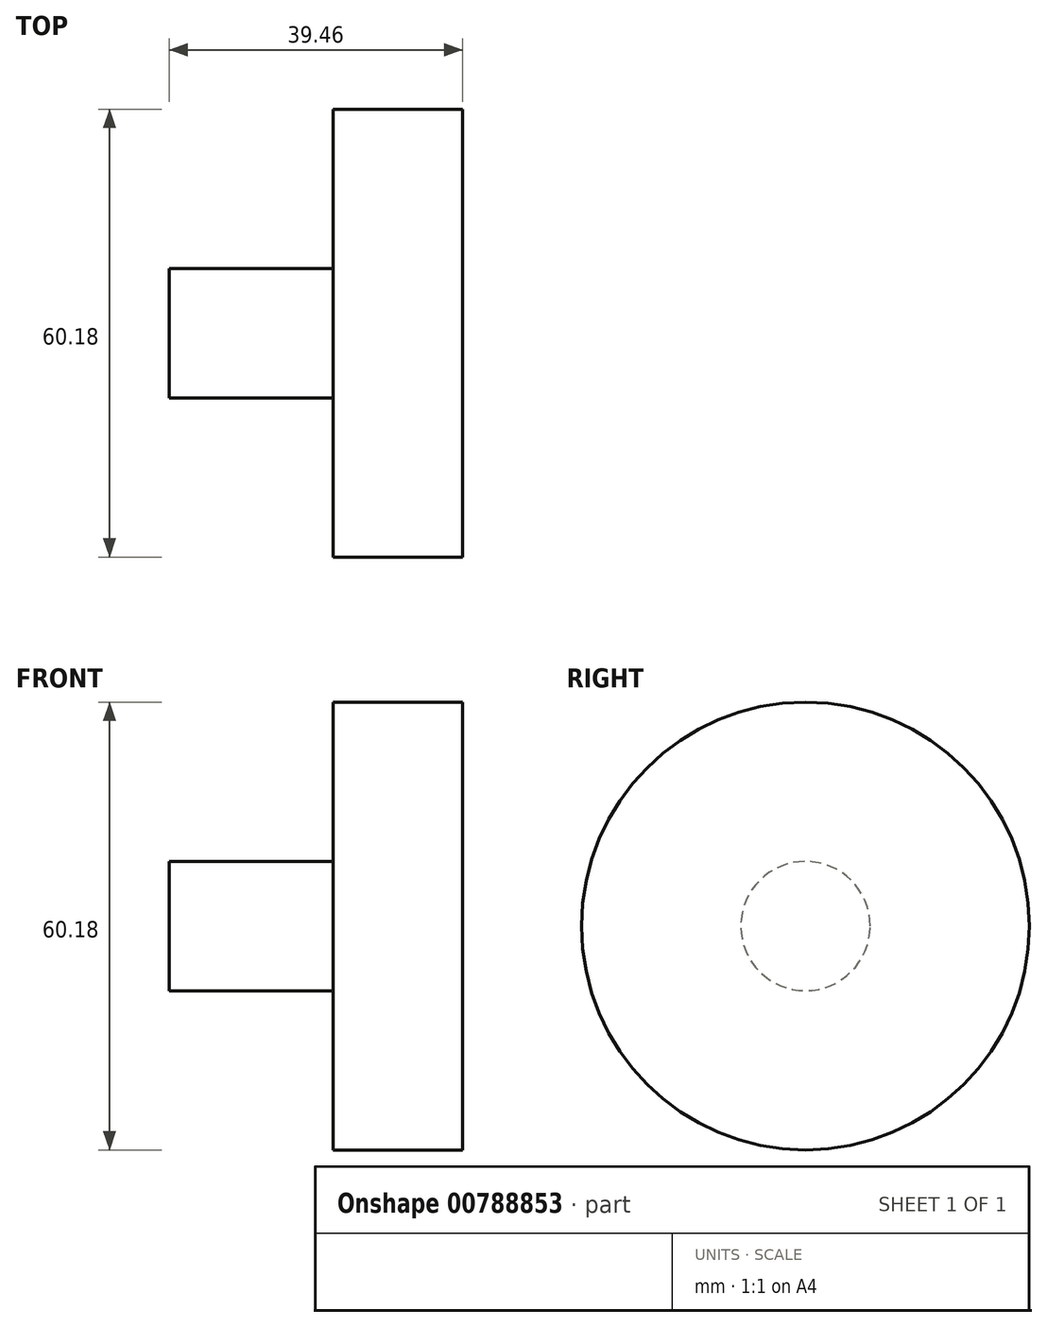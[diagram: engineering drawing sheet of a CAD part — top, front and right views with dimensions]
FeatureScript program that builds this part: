
annotation { "Feature Type Name" : "Feature", "Feature Type Description" : "" }
export const myFeature = defineFeature(function(context is Context, id is Id, definition is map)
    precondition{}
    {
        {
            var Q0;
            Q0=qCreatedBy(makeId("Front.planeOp"),FACE);
            var sketch = newSketch(context, id + "F0", { "sketchPlane" : qUnion([Q0])});
            skLineSegment(sketch, "E0", {"start": v(0, 0) * mm, "end": v(0, 8.7) * mm});
            skLineSegment(sketch, "E1", {"start": v(0, 8.7) * mm, "end": v(22.07, 8.7) * mm});
            skLineSegment(sketch, "E2", {"start": v(22.07, 8.7) * mm, "end": v(22.07, 30.1) * mm});
            skLineSegment(sketch, "E3", {"start": v(22.07, 30.1) * mm, "end": v(39.46, 30.1) * mm});
            skLineSegment(sketch, "E4", {"start": v(39.46, 30.1) * mm, "end": v(39.46, 0) * mm});
            skLineSegment(sketch, "E5", {"start": v(0, 0) * mm, "end": v(39.46, 0) * mm});
            skLineSegment(sketch, "E6", {"start": v(0, -4.24) * mm, "end": v(9.59, -4.24) * mm});
            skLineSegment(sketch, "E7", {"start": v(9.59, -4.24) * mm, "end": v(9.59, 0) * mm});
            skSolve(sketch);
        }
        {
            var Q0;
            Q0 = qSketchRegion(id + "F0", true);
            var Q1;
            Q1=sQuery(id+"F0.wireOp",EDGE,"E5");
            revolve(context, id + "F1", {"surfaceOperationType" : NewSurfaceOperationType.NEW, "entities" : qUnion([Q0]), "axis" : qUnion([Q1]), "revolveType" : RevolveType.FULL});
        }
    });
